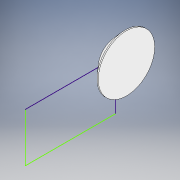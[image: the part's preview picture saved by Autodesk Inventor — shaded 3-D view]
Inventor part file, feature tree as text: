
AUTODESK INVENTOR PART (.ipt)
format: ipt  version: 2016 (Build 200138000, 138)  size: 146,432 bytes
history: native  units: mm
features: sketch x7, extrude x2, revolve x1
ambient origin geometry x8: Origin, YZ Plane, XZ Plane, XY Plane, X Axis, Y Axis, Z Axis, Center Point
bodies: Solid1 (feature_tree)
feature tree (10):
  revolve  "Revolution1"  [1 undecoded]
  extrude  "Extrusion1"  TaperAngle=90.0deg  [1 undecoded]
  sketch  "Sketch4"  dims[d11=24.0mm d12=7.5mm]
  sketch  "Sketch6"  dims[d13=7.4mm]
  sketch  "Sketch7"  dims[d14=10.0mm d15=0.0mm]
  extrude  "Extrusion2"  Depth=7.5mm
  sketch  "Sketch10"  dims[d18=3.0mm d19=0.0mm]
  sketch  "Sketch2"  dims[d4=65.0mm d5=22.0mm]
  sketch  "Sketch3"  dims[d6=40.3mm d7=90.0deg]
  sketch  "Sketch8"  dims[d17=5.0mm]
note: 2 required parameter values undecoded (feature->parameter linkage not recoverable at this tier; creation-order binding heuristic only, values carry confidence <= 0.55)